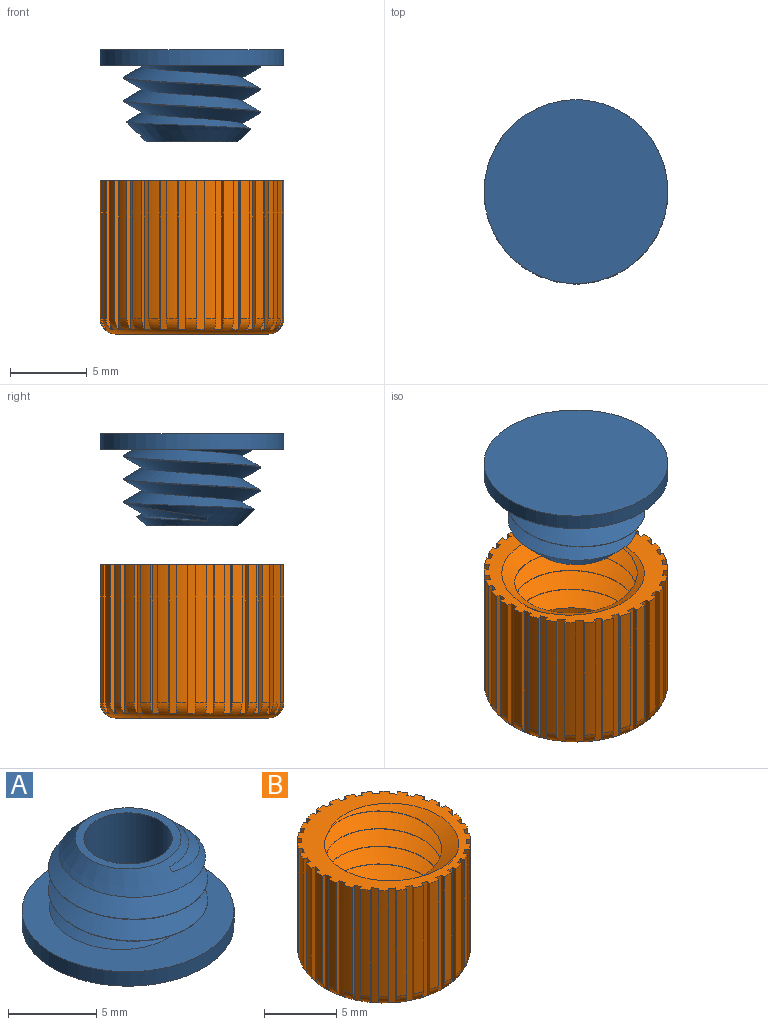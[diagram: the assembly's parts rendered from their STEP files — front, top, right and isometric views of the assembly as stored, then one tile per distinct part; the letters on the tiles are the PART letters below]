
ASSEMBLY  parts=2 mates=1
PART A: 12 faces, bbox 12x12x6.4 mm
  f0: cylinder r=4.5mm len=9mm, axis (0,0,1), area 2mm2, adj f5,f6,f7,f10
  f1: plane 6x6mm, normal (0,0,1), area 8.6mm2, adj f3,f4
  f2: plane 5x5mm, normal (0,0,1), area 19.6mm2, adj f3
  f3: cylinder r=2.5mm len=5mm, axis (0,0,1), area 62.8mm2, adj f1,f2
  f4: cone r=3mm half-angle=45deg, axis (0,0,-1), area 27.7mm2, adj f1,f5,f6,f7,f8
  f5: cone r=3mm half-angle=45deg, axis (0,0,-1), area 0mm2, adj f0,f4,f7
  f6: bspline ~10.39x9mm, area 97.7mm2, adj f0,f4,f7,f8,f10
  f7: bspline ~10.39x9mm, area 97.4mm2, adj f0,f4,f5,f6,f8,f10
  f8: plane 0.32x0.23mm, normal (1,0,0), area 0mm2, adj f4,f6,f7
  f9: cylinder r=6mm len=12mm, axis (0,0,-1), area 37.7mm2, adj f10,f11
  f10: plane 12x12mm, normal (0,0,1), area 65.5mm2, adj f0,f6,f7,f9
  f11: plane 12x12mm, normal (0,0,-1), area 113.1mm2, adj f9
PART B: 132 faces, bbox 14x14x11.8 mm
  f0: cylinder r=6mm len=9mm, axis (0,0,-1), area 6.5mm2, adj f30,f116,f120,f122
  f1: cylinder r=6mm len=9mm, axis (0,0,-1), area 6.5mm2, adj f30,f113,f117,f122
  f2: cylinder r=6mm len=9mm, axis (0,0,-1), area 6.5mm2, adj f30,f110,f114,f122
  f3: cylinder r=6mm len=9mm, axis (0,0,-1), area 6.5mm2, adj f30,f107,f111,f122
  f4: cylinder r=6mm len=9mm, axis (0,0,-1), area 6.5mm2, adj f30,f104,f108,f122
  f5: cylinder r=6mm len=9mm, axis (0,0,-1), area 6.5mm2, adj f30,f101,f105,f122
  f6: cylinder r=6mm len=9mm, axis (0,0,-1), area 6.5mm2, adj f30,f98,f102,f122
  f7: cylinder r=6mm len=9mm, axis (0,0,-1), area 6.5mm2, adj f30,f95,f99,f122
  f8: cylinder r=6mm len=9mm, axis (0,0,-1), area 6.5mm2, adj f30,f92,f96,f122
  f9: cylinder r=6mm len=9mm, axis (0,0,-1), area 6.5mm2, adj f30,f89,f93,f122
  f10: cylinder r=6mm len=9mm, axis (0,0,-1), area 6.5mm2, adj f30,f86,f90,f122
  f11: cylinder r=6mm len=9mm, axis (0,0,-1), area 6.5mm2, adj f30,f83,f87,f122
  f12: cylinder r=6mm len=9mm, axis (0,0,-1), area 6.5mm2, adj f30,f80,f84,f122
  f13: cylinder r=6mm len=9mm, axis (0,0,-1), area 6.5mm2, adj f30,f77,f81,f122
  f14: cylinder r=6mm len=9mm, axis (0,0,-1), area 6.5mm2, adj f30,f74,f78,f122
  f15: cylinder r=6mm len=9mm, axis (0,0,-1), area 6.5mm2, adj f30,f71,f75,f122
  f16: cylinder r=6mm len=9mm, axis (0,0,-1), area 6.5mm2, adj f30,f68,f72,f122
  f17: cylinder r=6mm len=9mm, axis (0,0,-1), area 6.5mm2, adj f30,f65,f69,f122
  f18: cylinder r=6mm len=9mm, axis (0,0,-1), area 6.5mm2, adj f30,f62,f66,f122
  f19: cylinder r=6mm len=9mm, axis (0,0,-1), area 6.5mm2, adj f30,f59,f63,f122
  f20: cylinder r=6mm len=9mm, axis (0,0,-1), area 6.5mm2, adj f30,f56,f60,f122
  f21: cylinder r=6mm len=9mm, axis (0,0,-1), area 6.5mm2, adj f30,f53,f57,f122
  f22: cylinder r=6mm len=9mm, axis (0,0,-1), area 6.5mm2, adj f30,f50,f54,f122
  f23: cylinder r=6mm len=9mm, axis (0,0,-1), area 6.5mm2, adj f30,f35,f51,f122
  f24: cylinder r=6mm len=9mm, axis (0,0,-1), area 6.5mm2, adj f30,f44,f48,f122
  f25: cylinder r=6mm len=9mm, axis (0,0,-1), area 6.5mm2, adj f30,f32,f45,f122
  f26: cylinder r=6mm len=9mm, axis (0,0,-1), area 6.5mm2, adj f30,f42,f47,f122
  f27: cylinder r=6mm len=9mm, axis (0,0,-1), area 6.5mm2, adj f30,f39,f41,f122
  f28: cylinder r=6mm len=9mm, axis (0,0,-1), area 6.5mm2, adj f30,f36,f38,f122
  f29: cylinder r=6mm len=9mm, axis (0,0,-1), area 6.5mm2, adj f30,f33,f119,f122
  f30: torus R=5mm, axis (0,0,1), area 43.2mm2, adj f0,f1,f2,f3,f4,f5,f6,f7
  f31: plane 10x10mm, normal (0,0,-1), area 78.5mm2, adj f30
  f32: plane 9.71x0.3mm, normal (-1,0.02,0), area 2.8mm2, adj f25,f30,f34,f122
  f33: plane 9.71x0.3mm, normal (0.99,-0.1,0), area 2.8mm2, adj f29,f30,f34,f122
  f34: plane 9.74x0.52mm, normal (-0.06,-1,0), area 4.9mm2, adj f30,f32,f33,f122
  f35: plane 9.71x0.26mm, normal (-0.51,-0.86,0), area 2.8mm2, adj f23,f30,f37,f122
  f36: plane 9.71x0.24mm, normal (0.59,0.81,0), area 2.8mm2, adj f28,f30,f37,f122
  f37: plane 9.74x0.44mm, normal (0.83,-0.55,0), area 4.9mm2, adj f30,f35,f36,f122
  f38: plane 9.71x0.22mm, normal (-0.68,-0.73,0), area 2.8mm2, adj f28,f30,f40,f122
  f39: plane 9.71x0.22mm, normal (0.74,0.67,0), area 2.8mm2, adj f27,f30,f40,f122
  f40: plane 9.74x0.37mm, normal (0.7,-0.71,0), area 4.9mm2, adj f30,f38,f39,f122
  f41: plane 9.71x0.25mm, normal (-0.82,-0.57,0), area 2.8mm2, adj f27,f30,f43,f122
  f42: plane 9.71x0.26mm, normal (0.87,0.5,0), area 2.8mm2, adj f26,f30,f43,f122
  f43: plane 9.74x0.44mm, normal (0.54,-0.84,0), area 4.9mm2, adj f30,f41,f42,f122
  f44: plane 9.71x0.29mm, normal (-0.98,-0.19,0), area 2.8mm2, adj f24,f30,f46,f122
  f45: plane 9.71x0.3mm, normal (0.99,0.1,0), area 2.8mm2, adj f25,f30,f46,f122
  f46: plane 9.74x0.51mm, normal (0.15,-0.99,0), area 4.9mm2, adj f30,f44,f45,f122
  f47: plane 9.71x0.28mm, normal (-0.92,-0.39,0), area 2.8mm2, adj f26,f30,f49,f122
  f48: plane 9.71x0.29mm, normal (0.95,0.31,0), area 2.8mm2, adj f24,f30,f49,f122
  f49: plane 9.74x0.49mm, normal (0.35,-0.94,0), area 4.9mm2, adj f30,f47,f48,f122
  f50: plane 9.71x0.28mm, normal (-0.32,-0.95,0), area 2.8mm2, adj f22,f30,f52,f122
  f51: plane 9.71x0.27mm, normal (0.41,0.91,0), area 2.8mm2, adj f23,f30,f52,f122
  f52: plane 9.74x0.48mm, normal (0.93,-0.37,0), area 4.9mm2, adj f30,f50,f51,f122
  f53: plane 9.71x0.3mm, normal (-0.12,-0.99,0), area 2.8mm2, adj f21,f30,f55,f122
  f54: plane 9.71x0.29mm, normal (0.21,0.98,0), area 2.8mm2, adj f22,f30,f55,f122
  f55: plane 9.74x0.51mm, normal (0.99,-0.16,0), area 4.9mm2, adj f30,f53,f54,f122
  f56: plane 9.71x0.3mm, normal (0.09,-1,0), area 2.8mm2, adj f20,f30,f58,f122
  f57: plane 9.71x0.3mm, normal (0,1,0), area 2.8mm2, adj f21,f30,f58,f122
  f58: plane 9.74x0.52mm, normal (1,0.04,0), area 4.9mm2, adj f30,f56,f57,f122
  f59: plane 9.71x0.29mm, normal (0.29,-0.96,0), area 2.8mm2, adj f19,f30,f61,f122
  f60: plane 9.71x0.29mm, normal (-0.21,0.98,0), area 2.8mm2, adj f20,f30,f61,f122
  f61: plane 9.74x0.5mm, normal (0.97,0.25,0), area 4.9mm2, adj f30,f59,f60,f122
  f62: plane 9.71x0.26mm, normal (0.49,-0.87,0), area 2.8mm2, adj f18,f30,f64,f122
  f63: plane 9.71x0.27mm, normal (-0.41,0.91,0), area 2.8mm2, adj f19,f30,f64,f122
  f64: plane 9.74x0.47mm, normal (0.89,0.45,0), area 4.9mm2, adj f30,f62,f63,f122
  f65: plane 9.71x0.23mm, normal (0.66,-0.75,0), area 2.8mm2, adj f17,f30,f67,f122
  f66: plane 9.71x0.24mm, normal (-0.59,0.81,0), area 2.8mm2, adj f18,f30,f67,f122
  f67: plane 9.74x0.41mm, normal (0.78,0.62,0), area 4.9mm2, adj f30,f65,f66,f122
  f68: plane 9.71x0.24mm, normal (0.8,-0.6,0), area 2.8mm2, adj f16,f30,f70,f122
  f69: plane 9.71x0.22mm, normal (-0.74,0.67,0), area 2.8mm2, adj f17,f30,f70,f122
  f70: plane 9.74x0.4mm, normal (0.64,0.77,0), area 4.9mm2, adj f30,f68,f69,f122
  f71: plane 9.71x0.27mm, normal (0.91,-0.42,0), area 2.8mm2, adj f15,f30,f73,f122
  f72: plane 9.71x0.26mm, normal (-0.87,0.5,0), area 2.8mm2, adj f16,f30,f73,f122
  f73: plane 9.74x0.46mm, normal (0.46,0.89,0), area 4.9mm2, adj f30,f71,f72,f122
  f74: plane 9.71x0.29mm, normal (0.97,-0.22,0), area 2.8mm2, adj f14,f30,f76,f122
  f75: plane 9.71x0.29mm, normal (-0.95,0.31,0), area 2.8mm2, adj f15,f30,f76,f122
  f76: plane 9.74x0.5mm, normal (0.27,0.96,0), area 4.9mm2, adj f30,f74,f75,f122
  f77: plane 9.71x0.3mm, normal (1,-0.02,0), area 2.8mm2, adj f13,f30,f79,f122
  f78: plane 9.71x0.3mm, normal (-0.99,0.1,0), area 2.8mm2, adj f14,f30,f79,f122
  f79: plane 9.74x0.52mm, normal (0.06,1,0), area 4.9mm2, adj f30,f77,f78,f122
  f80: plane 9.71x0.29mm, normal (0.98,0.19,0), area 2.8mm2, adj f12,f30,f82,f122
  f81: plane 9.71x0.3mm, normal (-0.99,-0.1,0), area 2.8mm2, adj f13,f30,f82,f122
  f82: plane 9.74x0.51mm, normal (-0.15,0.99,0), area 4.9mm2, adj f30,f80,f81,f122
  f83: plane 9.71x0.28mm, normal (0.92,0.39,0), area 2.8mm2, adj f11,f30,f85,f122
  f84: plane 9.71x0.29mm, normal (-0.95,-0.31,0), area 2.8mm2, adj f12,f30,f85,f122
  f85: plane 9.74x0.49mm, normal (-0.35,0.94,0), area 4.9mm2, adj f30,f83,f84,f122
  f86: plane 9.71x0.25mm, normal (0.82,0.57,0), area 2.8mm2, adj f10,f30,f88,f122
  f87: plane 9.71x0.26mm, normal (-0.87,-0.5,0), area 2.8mm2, adj f11,f30,f88,f122
  f88: plane 9.74x0.44mm, normal (-0.54,0.84,0), area 4.9mm2, adj f30,f86,f87,f122
  f89: plane 9.71x0.22mm, normal (0.68,0.73,0), area 2.8mm2, adj f9,f30,f91,f122
  f90: plane 9.71x0.22mm, normal (-0.74,-0.67,0), area 2.8mm2, adj f10,f30,f91,f122
  f91: plane 9.74x0.37mm, normal (-0.7,0.71,0), area 4.9mm2, adj f30,f89,f90,f122
  f92: plane 9.71x0.26mm, normal (0.51,0.86,0), area 2.8mm2, adj f8,f30,f94,f122
  f93: plane 9.71x0.24mm, normal (-0.59,-0.81,0), area 2.8mm2, adj f9,f30,f94,f122
  f94: plane 9.74x0.44mm, normal (-0.83,0.55,0), area 4.9mm2, adj f30,f92,f93,f122
  f95: plane 9.71x0.28mm, normal (0.32,0.95,0), area 2.8mm2, adj f7,f30,f97,f122
  f96: plane 9.71x0.27mm, normal (-0.41,-0.91,0), area 2.8mm2, adj f8,f30,f97,f122
  f97: plane 9.74x0.48mm, normal (-0.93,0.37,0), area 4.9mm2, adj f30,f95,f96,f122
  f98: plane 9.71x0.3mm, normal (0.12,0.99,0), area 2.8mm2, adj f6,f30,f100,f122
  f99: plane 9.71x0.29mm, normal (-0.21,-0.98,0), area 2.8mm2, adj f7,f30,f100,f122
  f100: plane 9.74x0.51mm, normal (-0.99,0.16,0), area 4.9mm2, adj f30,f98,f99,f122
  f101: plane 9.71x0.3mm, normal (-0.09,1,0), area 2.8mm2, adj f5,f30,f103,f122
  f102: plane 9.71x0.3mm, normal (0,-1,0), area 2.8mm2, adj f6,f30,f103,f122
  f103: plane 9.74x0.52mm, normal (-1,-0.04,0), area 4.9mm2, adj f30,f101,f102,f122
  f104: plane 9.71x0.29mm, normal (-0.29,0.96,0), area 2.8mm2, adj f4,f30,f106,f122
  f105: plane 9.71x0.29mm, normal (0.21,-0.98,0), area 2.8mm2, adj f5,f30,f106,f122
  f106: plane 9.74x0.5mm, normal (-0.97,-0.25,0), area 4.9mm2, adj f30,f104,f105,f122
  f107: plane 9.71x0.26mm, normal (-0.49,0.87,0), area 2.8mm2, adj f3,f30,f109,f122
  f108: plane 9.71x0.27mm, normal (0.41,-0.91,0), area 2.8mm2, adj f4,f30,f109,f122
  f109: plane 9.74x0.47mm, normal (-0.89,-0.45,0), area 4.9mm2, adj f30,f107,f108,f122
  f110: plane 9.71x0.23mm, normal (-0.66,0.75,0), area 2.8mm2, adj f2,f30,f112,f122
  f111: plane 9.71x0.24mm, normal (0.59,-0.81,0), area 2.8mm2, adj f3,f30,f112,f122
  f112: plane 9.74x0.41mm, normal (-0.78,-0.62,0), area 4.9mm2, adj f30,f110,f111,f122
  f113: plane 9.71x0.24mm, normal (-0.8,0.6,0), area 2.8mm2, adj f1,f30,f115,f122
  f114: plane 9.71x0.22mm, normal (0.74,-0.67,0), area 2.8mm2, adj f2,f30,f115,f122
  f115: plane 9.74x0.4mm, normal (-0.64,-0.77,0), area 4.9mm2, adj f30,f113,f114,f122
  f116: plane 9.71x0.27mm, normal (-0.91,0.42,0), area 2.8mm2, adj f0,f30,f118,f122
  f117: plane 9.71x0.26mm, normal (0.87,-0.5,0), area 2.8mm2, adj f1,f30,f118,f122
  f118: plane 9.74x0.46mm, normal (-0.46,-0.89,0), area 4.9mm2, adj f30,f116,f117,f122
  f119: plane 9.71x0.29mm, normal (-0.97,0.22,0), area 2.8mm2, adj f29,f30,f121,f122
  f120: plane 9.71x0.29mm, normal (0.95,-0.31,0), area 2.8mm2, adj f0,f30,f121,f122
  f121: plane 9.74x0.5mm, normal (-0.27,-0.96,0), area 4.9mm2, adj f30,f119,f120,f122
  f122: plane 13.02x13.02mm, normal (0,0,1), area 40.5mm2, adj f0,f1,f2,f3,f4,f5,f6,f7
  f123: plane 8x8mm, normal (0,0,1), area 50.3mm2, adj f128
  f124: cylinder r=4mm len=6mm, axis (0,0,-1), area 0.2mm2, adj f122,f125,f130,f131
  f125: cylinder r=4mm len=8mm, axis (0,0,-1), area 0.5mm2, adj f124,f126,f130,f131
  f126: cylinder r=4mm len=8mm, axis (0,0,-1), area 0.5mm2, adj f125,f127,f130,f131
  f127: cylinder r=4mm len=8mm, axis (0,0,-1), area 0.5mm2, adj f126,f128,f130,f131
  f128: cylinder r=4mm len=8mm, axis (0,0,-1), area 57.1mm2, adj f123,f127,f129,f131
  f129: plane 1.48x1.28mm, normal (0,1,0), area 0.9mm2, adj f128,f130,f131
  f130: bspline ~12.2x10.56mm, area 154.9mm2, adj f122,f124,f125,f126,f127,f129,f131
  f131: bspline ~12.2x10.56mm, area 175.4mm2, adj f122,f124,f125,f126,f127,f128,f129,f130
PLACE A rot(axis=(0.59,0.81,0),180deg) t=(-3.03,5.62,18.54)mm
PLACE B rot(axis=(0,0,-1),99deg) t=(-3.03,5.62,0)mm
MATE cylindrical A.f0 <-> B.f0  axis (0,0,-1) through (-3.03,5.62,14.54)mm
